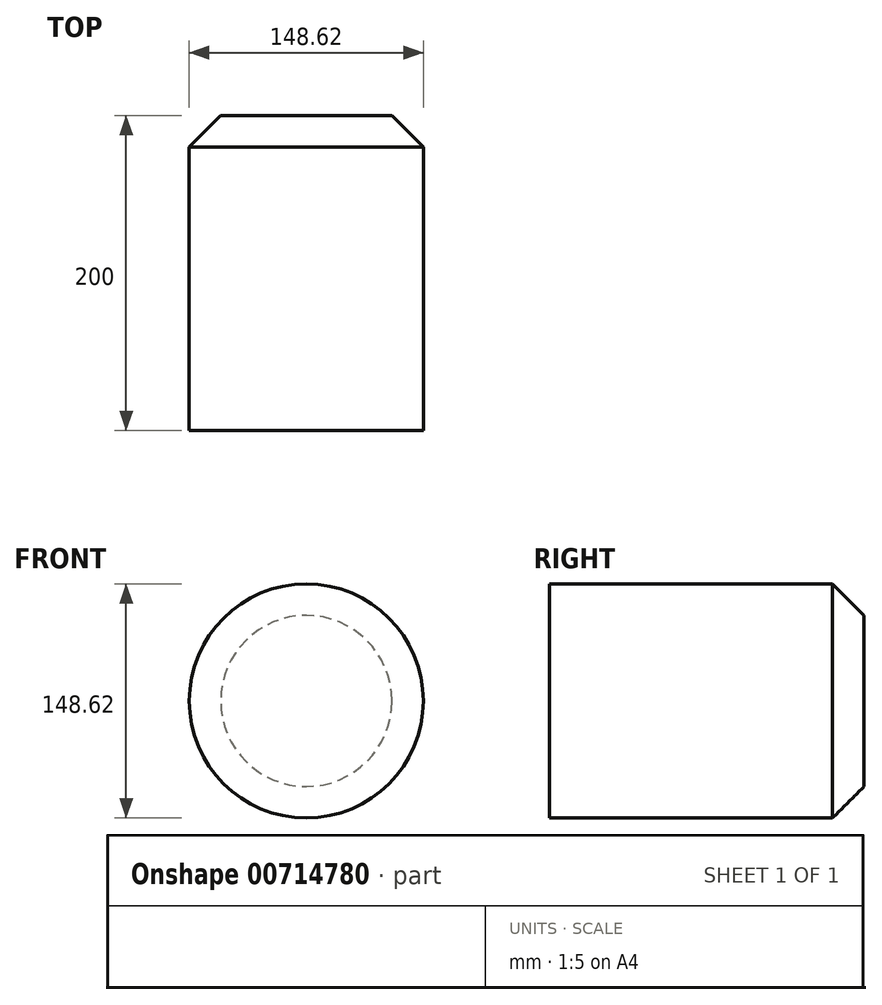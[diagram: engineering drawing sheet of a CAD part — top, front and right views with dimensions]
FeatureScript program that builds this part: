
annotation { "Feature Type Name" : "Feature", "Feature Type Description" : "" }
export const myFeature = defineFeature(function(context is Context, id is Id, definition is map)
    precondition{}
    {
        {
            var Q0;
            Q0=qCreatedBy(makeId("Front.planeOp"),FACE);
            var sketch = newSketch(context, id + "F0", { "sketchPlane" : qUnion([Q0])});
            skCircle(sketch, "E0", {"center": v(0, 0) * mm, "radius": 74.3 * mm});
            skSolve(sketch);
        }
        {
            var Q0;
            Q0=makeQuery(id+"F0.imprint","IMPRINT",FACE,{"disambiguationData":[TD([[makeQuery(id+"F0.imprint","IMPRINT",EDGE,{"derivedFrom":sQuery(id+"F0.wireOp",EDGE,"E0")}),1.0]])]});
            var sketch = newSketch(context, id + "F1", { "sketchPlane" : qUnion([Q0])});
            skSolve(sketch);
        }
        {
            var Q0;
            Q0=makeQuery(id+"F1.imprint","IMPRINT",FACE,{"disambiguationData":[TD([[makeQuery(id+"F1.imprint","IMPRINT",EDGE,{"derivedFrom":makeQuery(id+"F0.imprint","IMPRINT",EDGE,{"derivedFrom":sQuery(id+"F0.wireOp",EDGE,"E0")})}),1.0]])]});
            extrude(context, id + "F2", {"entities" : qUnion([Q0]), "oppositeDirection" : true, "depth" : 200 * mm, "offsetDistance" : 25 * mm});
        }
        {
            var Q0;
            Q0=makeQuery(id+"F2.opExtrude","CAP_EDGE",EDGE,{"disambiguationData":[OSD([sQuery(id+"F0.wireOp",EDGE,"E0")])],"isStart":false});
            chamfer(context, id + "F3", {"entities" : qUnion([Q0]), "width" : 20 * mm, "tangentPropagation" : true});
        }
    });
